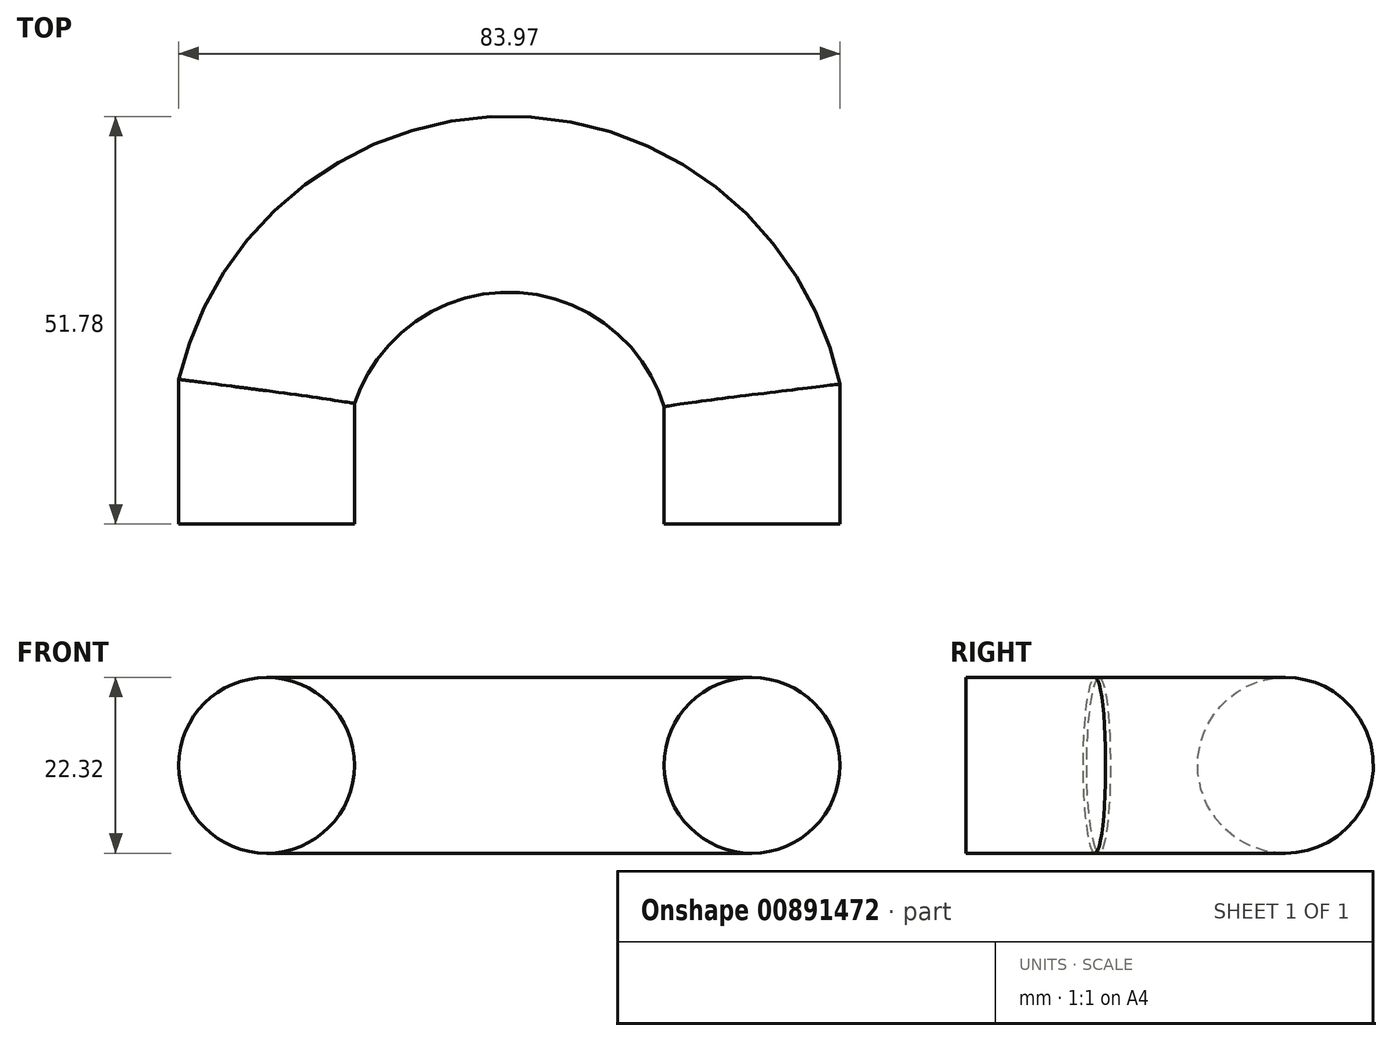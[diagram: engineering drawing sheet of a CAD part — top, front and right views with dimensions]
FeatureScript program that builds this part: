
annotation { "Feature Type Name" : "Feature", "Feature Type Description" : "" }
export const myFeature = defineFeature(function(context is Context, id is Id, definition is map)
    precondition{}
    {
        {
            var Q0;
            Q0=qCreatedBy(makeId("Top.planeOp"),FACE);
            var sketch = newSketch(context, id + "F0", { "sketchPlane" : qUnion([Q0])});
            skLineSegment(sketch, "E0", {"start": v(-34.4, 0) * mm, "end": v(-34.4, 16.92) * mm});
            skLineSegment(sketch, "E1", {"start": v(27.24, 0) * mm, "end": v(27.24, 16.42) * mm});
            skArc(sketch, "E2", {"start": v(27.24, 16.42) * mm, "mid": v(-3.39, 40.62) * mm, "end": v(-34.4, 16.92) * mm});
            skSolve(sketch);
        }
        {
            var Q0;
            Q0=qCreatedBy(makeId("Front.planeOp"),FACE);
            var sketch = newSketch(context, id + "F1", { "sketchPlane" : qUnion([Q0])});
            skCircle(sketch, "E3", {"center": v(-34.4, 0) * mm, "radius": 11.16 * mm});
            skSolve(sketch);
        }
        {
            var Q0;
            Q0=makeQuery(id+"F1.imprint","IMPRINT",FACE,{"disambiguationData":[TD([[makeQuery(id+"F1.imprint","IMPRINT",EDGE,{"derivedFrom":sQuery(id+"F1.wireOp",EDGE,"E3")}),1.0]])]});
            var Q1;
            Q1=sQuery(id+"F0.wireOp",EDGE,"E0");
            var Q2;
            Q2=sQuery(id+"F0.wireOp",EDGE,"E2");
            var Q3;
            Q3=sQuery(id+"F0.wireOp",EDGE,"E1");
            sweep(context, id + "F2", {"profiles" : qUnion([Q0]), "path" : qUnion([Q1, Q2, Q3])});
        }
    });
